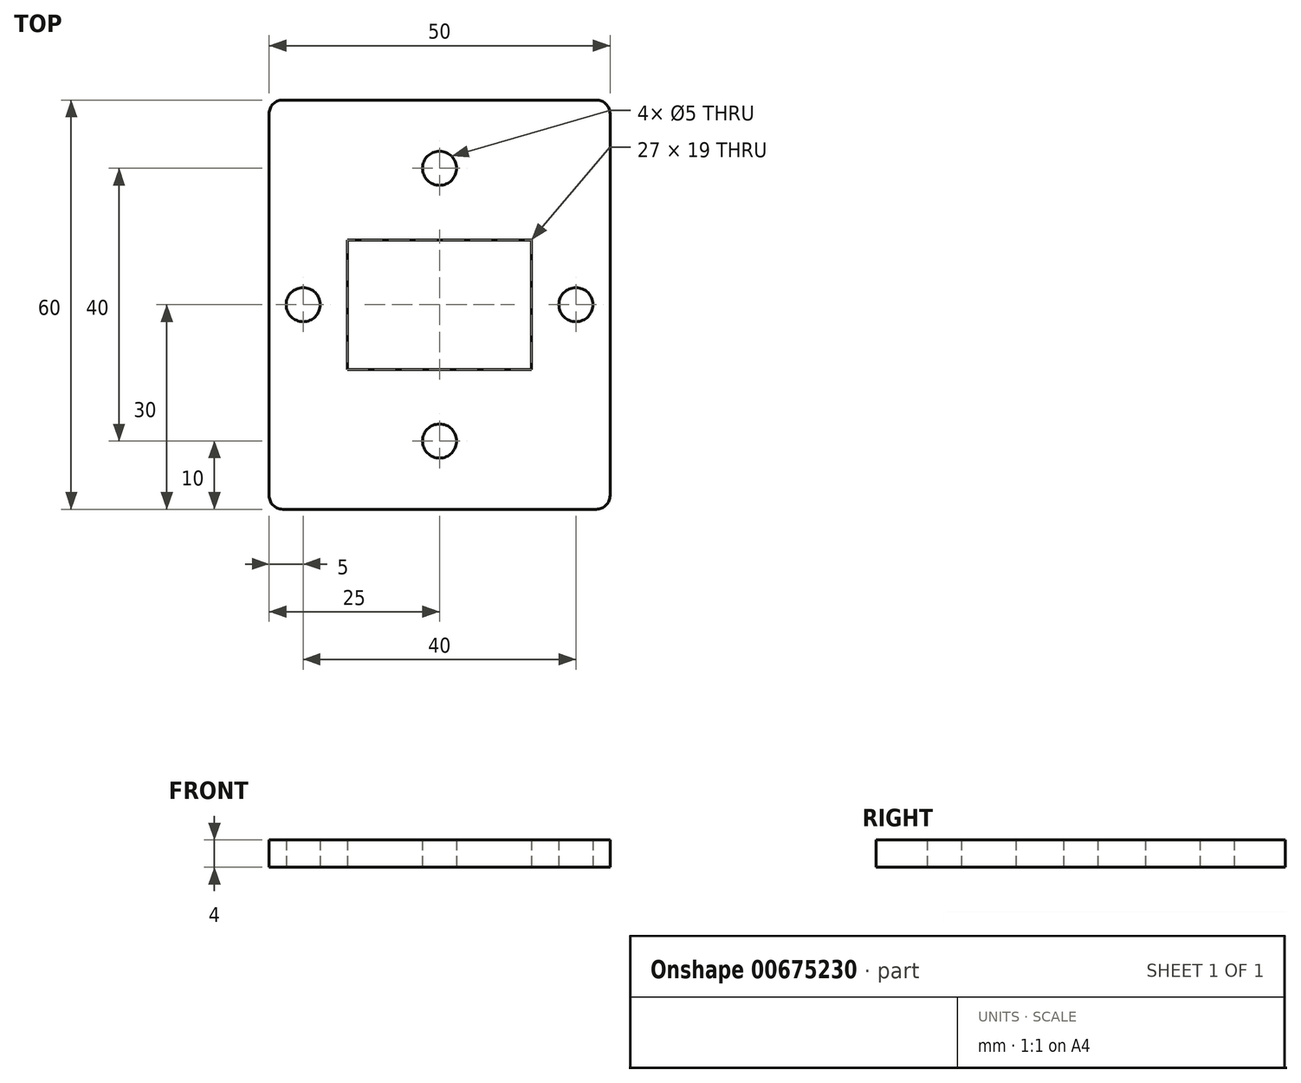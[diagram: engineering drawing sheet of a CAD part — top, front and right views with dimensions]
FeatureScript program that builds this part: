
annotation { "Feature Type Name" : "Feature", "Feature Type Description" : "" }
export const myFeature = defineFeature(function(context is Context, id is Id, definition is map)
    precondition{}
    {
        {
            var Q0;
            Q0=qCreatedBy(makeId("Top.planeOp"),FACE);
            var sketch = newSketch(context, id + "F0", { "sketchPlane" : qUnion([Q0])});
            skLineSegment(sketch, "E0.bottom", {"start": v(25, -30) * mm, "end": v(-25, -30) * mm});
            skLineSegment(sketch, "E0.top", {"start": v(25, 30) * mm, "end": v(-25, 30) * mm});
            skLineSegment(sketch, "E0.left", {"start": v(25, -30) * mm, "end": v(25, 30) * mm});
            skLineSegment(sketch, "E0.right", {"start": v(-25, -30) * mm, "end": v(-25, 30) * mm});
            skPoint(sketch, "E0.middle", {"position": v(0, 0) * mm});
            skCircle(sketch, "E1", {"center": v(0, 20) * mm, "radius": 2.5 * mm});
            skCircle(sketch, "E2", {"center": v(0, -20) * mm, "radius": 2.5 * mm});
            skCircle(sketch, "E3", {"center": v(-20, 0) * mm, "radius": 2.5 * mm});
            skCircle(sketch, "E4", {"center": v(20, 0) * mm, "radius": 2.5 * mm});
            skLineSegment(sketch, "E5.bottom", {"start": v(13.5, -9.5) * mm, "end": v(-13.5, -9.5) * mm});
            skLineSegment(sketch, "E5.top", {"start": v(13.5, 9.5) * mm, "end": v(-13.5, 9.5) * mm});
            skLineSegment(sketch, "E5.left", {"start": v(13.5, -9.5) * mm, "end": v(13.5, 9.5) * mm});
            skLineSegment(sketch, "E5.right", {"start": v(-13.5, -9.5) * mm, "end": v(-13.5, 9.5) * mm});
            skSolve(sketch);
        }
        {
            var Q0;
            Q0=makeQuery(id+"F0.imprint","IMPRINT",FACE,{"disambiguationData":[TD([[makeQuery(id+"F0.imprint","IMPRINT",EDGE,{"derivedFrom":sQuery(id+"F0.wireOp",EDGE,"E0.bottom")}),-1.0]])]});
            extrude(context, id + "F1", {"entities" : qUnion([Q0]), "depth" : 4 * mm, "offsetDistance" : 25 * mm});
        }
        {
            var Q0;
            Q0=makeQuery(id+"FslTN8SEal1Xb2Q_2.opExtrude","SWEPT_EDGE",EDGE,{"disambiguationData":[OSD([sQuery(id+"FC4kE9HebCvjoLd_1.wireOp",EDGE,"d27a3ac5-fa86-4e87-92a8-88ad98124e66.0"),sQuery(id+"FC4kE9HebCvjoLd_1.wireOp",EDGE,"d27a3ac5-fa86-4e87-92a8-88ad98124e66.1")])]});
            var Q1;
            Q1=makeQuery(id+"F1.opExtrude","SWEPT_EDGE",EDGE,{"disambiguationData":[OSD([sQuery(id+"F0.wireOp",EDGE,"E0.top"),sQuery(id+"F0.wireOp",EDGE,"E0.left")])]});
            var Q2;
            Q2=makeQuery(id+"FslTN8SEal1Xb2Q_2.opExtrude","SWEPT_EDGE",EDGE,{"disambiguationData":[OSD([sQuery(id+"FC4kE9HebCvjoLd_1.wireOp",EDGE,"d27a3ac5-fa86-4e87-92a8-88ad98124e66.0"),sQuery(id+"FC4kE9HebCvjoLd_1.wireOp",EDGE,"d27a3ac5-fa86-4e87-92a8-88ad98124e66.3")])]});
            var Q3;
            Q3=makeQuery(id+"F1.opExtrude","SWEPT_EDGE",EDGE,{"disambiguationData":[OSD([sQuery(id+"F0.wireOp",EDGE,"E0.bottom"),sQuery(id+"F0.wireOp",EDGE,"E0.left")])]});
            var Q4;
            Q4=makeQuery(id+"FslTN8SEal1Xb2Q_2.opExtrude","SWEPT_EDGE",EDGE,{"disambiguationData":[OSD([sQuery(id+"FC4kE9HebCvjoLd_1.wireOp",EDGE,"d27a3ac5-fa86-4e87-92a8-88ad98124e66.1"),sQuery(id+"FC4kE9HebCvjoLd_1.wireOp",EDGE,"d27a3ac5-fa86-4e87-92a8-88ad98124e66.2")])]});
            var Q5;
            Q5=makeQuery(id+"F1.opExtrude","SWEPT_EDGE",EDGE,{"disambiguationData":[OSD([sQuery(id+"F0.wireOp",EDGE,"E0.top"),sQuery(id+"F0.wireOp",EDGE,"E0.right")])]});
            var Q6;
            Q6=makeQuery(id+"FslTN8SEal1Xb2Q_2.opExtrude","SWEPT_EDGE",EDGE,{"disambiguationData":[OSD([sQuery(id+"FC4kE9HebCvjoLd_1.wireOp",EDGE,"d27a3ac5-fa86-4e87-92a8-88ad98124e66.2"),sQuery(id+"FC4kE9HebCvjoLd_1.wireOp",EDGE,"d27a3ac5-fa86-4e87-92a8-88ad98124e66.3")])]});
            var Q7;
            Q7=makeQuery(id+"F1.opExtrude","SWEPT_EDGE",EDGE,{"disambiguationData":[OSD([sQuery(id+"F0.wireOp",EDGE,"E0.bottom"),sQuery(id+"F0.wireOp",EDGE,"E0.right")])]});
            fillet(context, id + "F2", {"entities" : qUnion([Q0, Q1, Q2, Q3, Q4, Q5, Q6, Q7]), "radius" : 2 * mm, "tangentPropagation" : true, "allowEdgeOverflow" : false});
        }
    });
